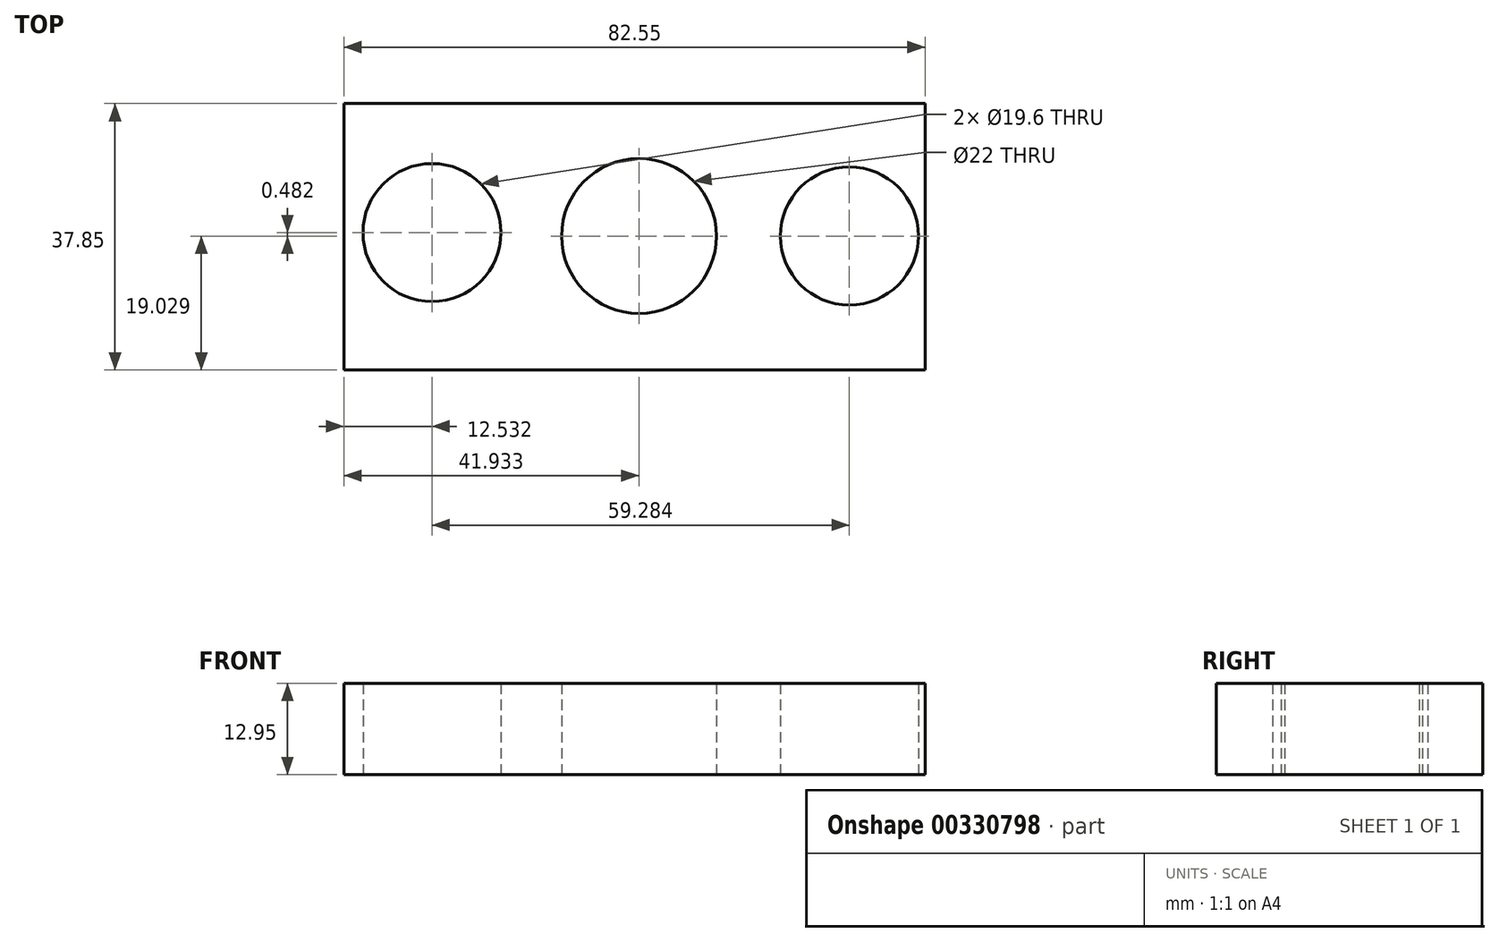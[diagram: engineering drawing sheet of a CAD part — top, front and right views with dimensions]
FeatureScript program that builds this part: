
annotation { "Feature Type Name" : "Feature", "Feature Type Description" : "" }
export const myFeature = defineFeature(function(context is Context, id is Id, definition is map)
    precondition{}
    {
        {
            var Q0;
            Q0=qCreatedBy(makeId("Top.planeOp"),FACE);
            var sketch = newSketch(context, id + "F0", { "sketchPlane" : qUnion([Q0])});
            skLineSegment(sketch, "E0.bottom", {"start": v(0, 0) * mm, "end": v(82.55, 0) * mm});
            skLineSegment(sketch, "E0.top", {"start": v(0, 38.1) * mm, "end": v(82.55, 38.1) * mm});
            skLineSegment(sketch, "E0.left", {"start": v(0, 0) * mm, "end": v(0, 38.1) * mm});
            skLineSegment(sketch, "E0.right", {"start": v(82.55, 0) * mm, "end": v(82.55, 38.1) * mm});
            skCircle(sketch, "E1", {"center": v(41.93, 19.28) * mm, "radius": 11 * mm});
            skCircle(sketch, "E2", {"center": v(71.82, 19.28) * mm, "radius": 9.8 * mm});
            skCircle(sketch, "E3", {"center": v(12.53, 19.76) * mm, "radius": 9.8 * mm});
            skSolve(sketch);
        }
        {
            var Q0;
            Q0=makeQuery(id+"F0.imprint","IMPRINT",FACE,{"disambiguationData":[TD([[makeQuery(id+"F0.imprint","IMPRINT",EDGE,{"derivedFrom":sQuery(id+"F0.wireOp",EDGE,"E0.bottom")}),1.0]])]});
            extrude(context, id + "F1", {"entities" : qUnion([Q0]), "depth" : 12.95 * mm});
        }
        {
            var Q0;
            Q0=makeQuery(id+"F1.opExtrude","SWEPT_FACE",FACE,{"disambiguationData":[OSD([sQuery(id+"F0.wireOp",EDGE,"E0.bottom")])]});
            extrude(context, id + "F2", {"entities" : qUnion([Q0]), "operationType" : NewBodyOperationType.REMOVE, "oppositeDirection" : true, "depth" : 0.25 * mm});
        }
    });
